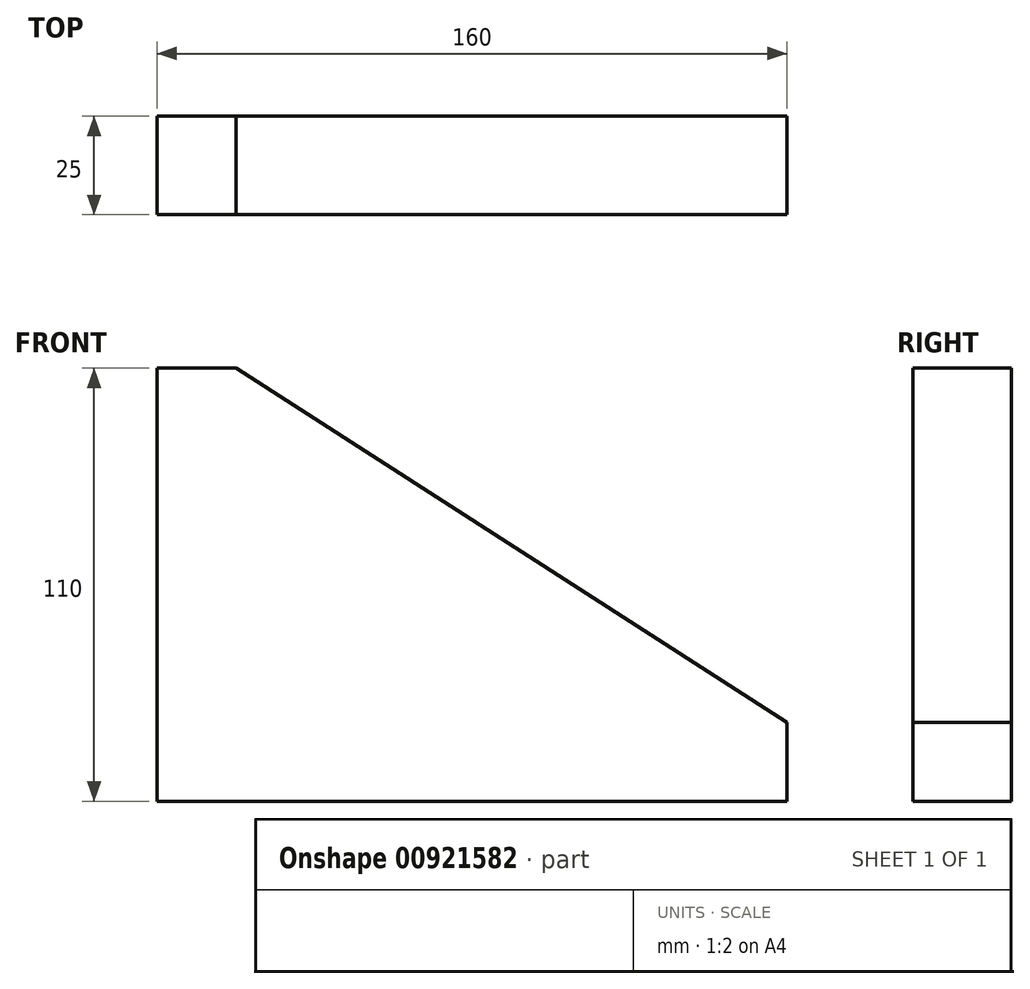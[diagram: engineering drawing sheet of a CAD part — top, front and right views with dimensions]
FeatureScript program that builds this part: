
annotation { "Feature Type Name" : "Feature", "Feature Type Description" : "" }
export const myFeature = defineFeature(function(context is Context, id is Id, definition is map)
    precondition{}
    {
        {
            var Q0;
            Q0=qCreatedBy(makeId("Front.planeOp"),FACE);
            var sketch = newSketch(context, id + "F0", { "sketchPlane" : qUnion([Q0])});
            skLineSegment(sketch, "E0", {"start": v(-103.39, 53.43) * mm, "end": v(-103.39, -56.57) * mm});
            skLineSegment(sketch, "E1", {"start": v(-103.39, -56.57) * mm, "end": v(56.61, -56.57) * mm});
            skLineSegment(sketch, "E2", {"start": v(56.61, -36.57) * mm, "end": v(-83.39, 53.43) * mm});
            skLineSegment(sketch, "E3", {"start": v(-103.39, 53.43) * mm, "end": v(-83.39, 53.43) * mm});
            skLineSegment(sketch, "E4", {"start": v(56.61, -36.57) * mm, "end": v(56.61, -56.57) * mm});
            skSolve(sketch);
        }
        {
            var Q0;
            Q0 = qSketchRegion(id + "F0", true);
            extrude(context, id + "F1", {"entities" : qUnion([Q0]), "depth" : 25 * mm, "offsetDistance" : 25 * mm});
        }
        {
            var Q0;
            Q0 = qSketchRegion(id + "F0", true);
            extrude(context, id + "F2", {"entities" : qUnion([Q0]), "operationType" : NewBodyOperationType.ADD, "depth" : 25 * mm, "offsetDistance" : 25 * mm});
        }
        {
            var Q0;
            Q0 = qSketchRegion(id + "F0", true);
            extrude(context, id + "F3", {"entities" : qUnion([Q0]), "operationType" : NewBodyOperationType.ADD, "depth" : 25 * mm, "offsetDistance" : 25 * mm});
        }
        {
            var Q0;
            Q0 = qSketchRegion(id + "F0", true);
            extrude(context, id + "F4", {"entities" : qUnion([Q0]), "operationType" : NewBodyOperationType.ADD, "depth" : 25 * mm, "offsetDistance" : 25 * mm});
        }
        {
            var Q0;
            Q0 = qSketchRegion(id + "F0", true);
            extrude(context, id + "F5", {"entities" : qUnion([Q0]), "operationType" : NewBodyOperationType.ADD, "depth" : 25 * mm, "offsetDistance" : 25 * mm});
        }
    });
